# Revit family: FT Pyros LED_2020
name_source: partatom
category: Lighting Fixtures
units: mm (PartAtom-declared; Revit-internal decimal feet)

## family parameters
Always vertical = Yes
Cut with Voids When Loaded = No
Light Source = Yes
OmniClass Number = 23.80.70.00
OmniClass Title = Lighting
Part Type = Normal
Room Calculation Point = No
Round Connector Dimension = Use Diameter
Shared = No
Work Plane-Based = No

## types (6) — shared parameters
Color Filter = 16777215
Description = https://www.airfal.com
Dimming Lamp Color Temperature Shift = <None>
EX Area = II2GD Ex db op is IIB+H2 T6 Gb Ex op is tb IIIC T85 ºC Dc
Emergency system = Yes
Emit from Line Length = 609.6 mm  [stored 2 ft]
IK = IK10
IP = IP66
Led Module = Yes
MacAdam Ellipse = 3/4
Photobiological risk group = RG1
Tilt Angle = 90.00°
URL = https://www.airfal.com
Unify glade rating = UGR<19
Useful life = L70B50>50000
zero-valued in all types: Default Elevation

## per-type parameters (varying)
| type | L | Photometric Web File | Size | Watts |
| PY113 | 748 mm  [stored 2.45407 ft] | PY113 PYROS LED  600mm 2150lm 14W.IES | 600 mm | 14 W |
| PY123 | 748 mm  [stored 2.45407 ft] | PY123 PYROS LED 600mm 4300lm 28W.IES | 600 mm | 28 W |
| PY213 | 1357 mm  [stored 4.4521 ft] | PY213 PYROS LED  1200mm 4300lm 28W.IES | 1200 mm | 28 W |
| PY223 | 1357 mm  [stored 4.4521 ft] | PY223 PYROS LED 1200mm 8600lm 55W.IES | 1200 mm | 55 W |
| PY313 | 1659 mm  [stored 5.44291 ft] | PY313 PYROS LED  1500mm 5370lm 35W.IES | 1500 mm  [stored 4.92126 ft] | 35 W |
| PY323 | 1659 mm  [stored 5.44291 ft] | PY323 PYROS LED  1500mm 10740lm 70W.IES | 1500 mm  [stored 4.92126 ft] | 70 W |

note: [stored X ft] marks values corroborated as IEEE doubles in the binary element streams (Revit-internal decimal feet)

## geometry (parser evidence)
native form markers: Blend x8, Sweep x19
no freeform markers — native parametric forms only
